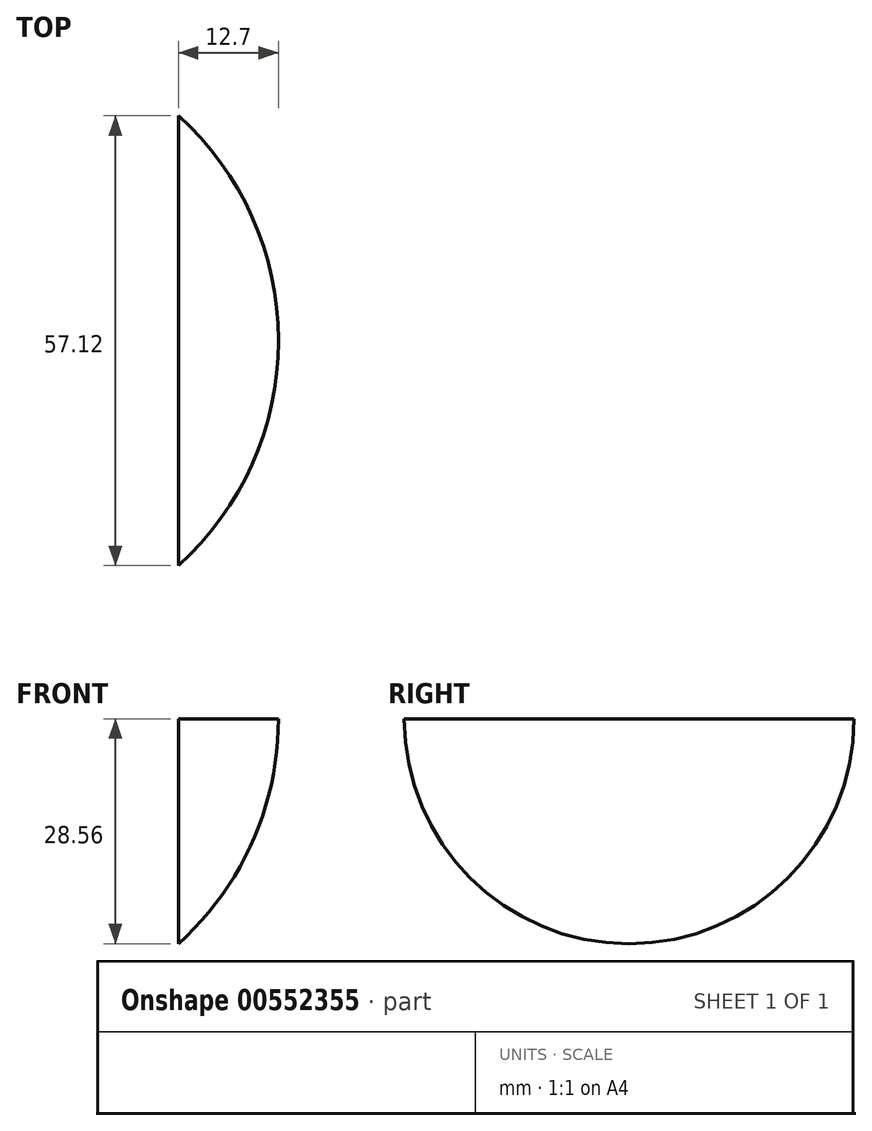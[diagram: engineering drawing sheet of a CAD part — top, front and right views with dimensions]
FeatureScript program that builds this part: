
annotation { "Feature Type Name" : "Feature", "Feature Type Description" : "" }
export const myFeature = defineFeature(function(context is Context, id is Id, definition is map)
    precondition{}
    {
        {
            var Q0;
            Q0=qCreatedBy(makeId("Top.planeOp"),FACE);
            var sketch = newSketch(context, id + "F0", { "sketchPlane" : qUnion([Q0])});
            skArc(sketch, "E0", {"start": v(-76.27, 0) * mm, "mid": v(-38.13, -38.28) * mm, "end": v(0, 0) * mm});
            skLineSegment(sketch, "E1", {"start": v(-76.27, 0) * mm, "end": v(0, 0) * mm});
            skSolve(sketch);
        }
        {
            var Q0;
            Q0 = qSketchRegion(id + "F0", true);
            var Q1;
            Q1=sQuery(id+"F0.wireOp",EDGE,"E1");
            revolve(context, id + "F1", {"entities" : qUnion([Q0]), "axis" : qUnion([Q1]), "revolveType" : RevolveType.FULL});
        }
        {
            var Q0;
            Q0=qCreatedBy(makeId("Right.planeOp"),FACE);
            var sketch = newSketch(context, id + "F2", { "sketchPlane" : qUnion([Q0])});
            skArc(sketch, "E2", {"start": v(-29.07, 0) * mm, "mid": v(0, -29.07) * mm, "end": v(29.07, 0) * mm});
            skLineSegment(sketch, "E3", {"start": v(-29.07, 0) * mm, "end": v(29.07, 0) * mm});
            skSolve(sketch);
        }
        {
            var Q0;
            Q0 = qSketchRegion(id + "F2", true);
            extrude(context, id + "F3", {"entities" : qUnion([Q0]), "operationType" : NewBodyOperationType.REMOVE, "endBound" : BoundingType.SYMMETRIC, "oppositeDirection" : true, "depth" : 25.4 * mm, "offsetDistance" : 25.4 * mm});
        }
    });
